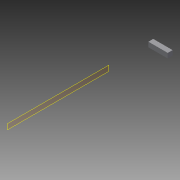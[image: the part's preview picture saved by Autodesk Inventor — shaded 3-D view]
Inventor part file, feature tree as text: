
AUTODESK INVENTOR PART (.ipt)
format: ipt  version: 2015 (Build 190159000, 159)  size: 69,632 bytes
history: native  units: in
note: dims shown in document units (in); Inventor stores cm internally (conversion verified against a paired STEP export)
features: plane x1, extrude x1, sketch x1
ambient origin geometry x8: Origin, YZ Plane, XZ Plane, XY Plane, X Axis, Y Axis, Z Axis, Center Point
bodies: Solid1 (feature_tree)
feature tree (3):
  plane  "Work Plane1"
  extrude  "Extrusion1"  Depth=0.75in
  sketch  "Sketch1"  dims[d0=0.75in d1=0.75in d2=3.0in d3=0.0in]
